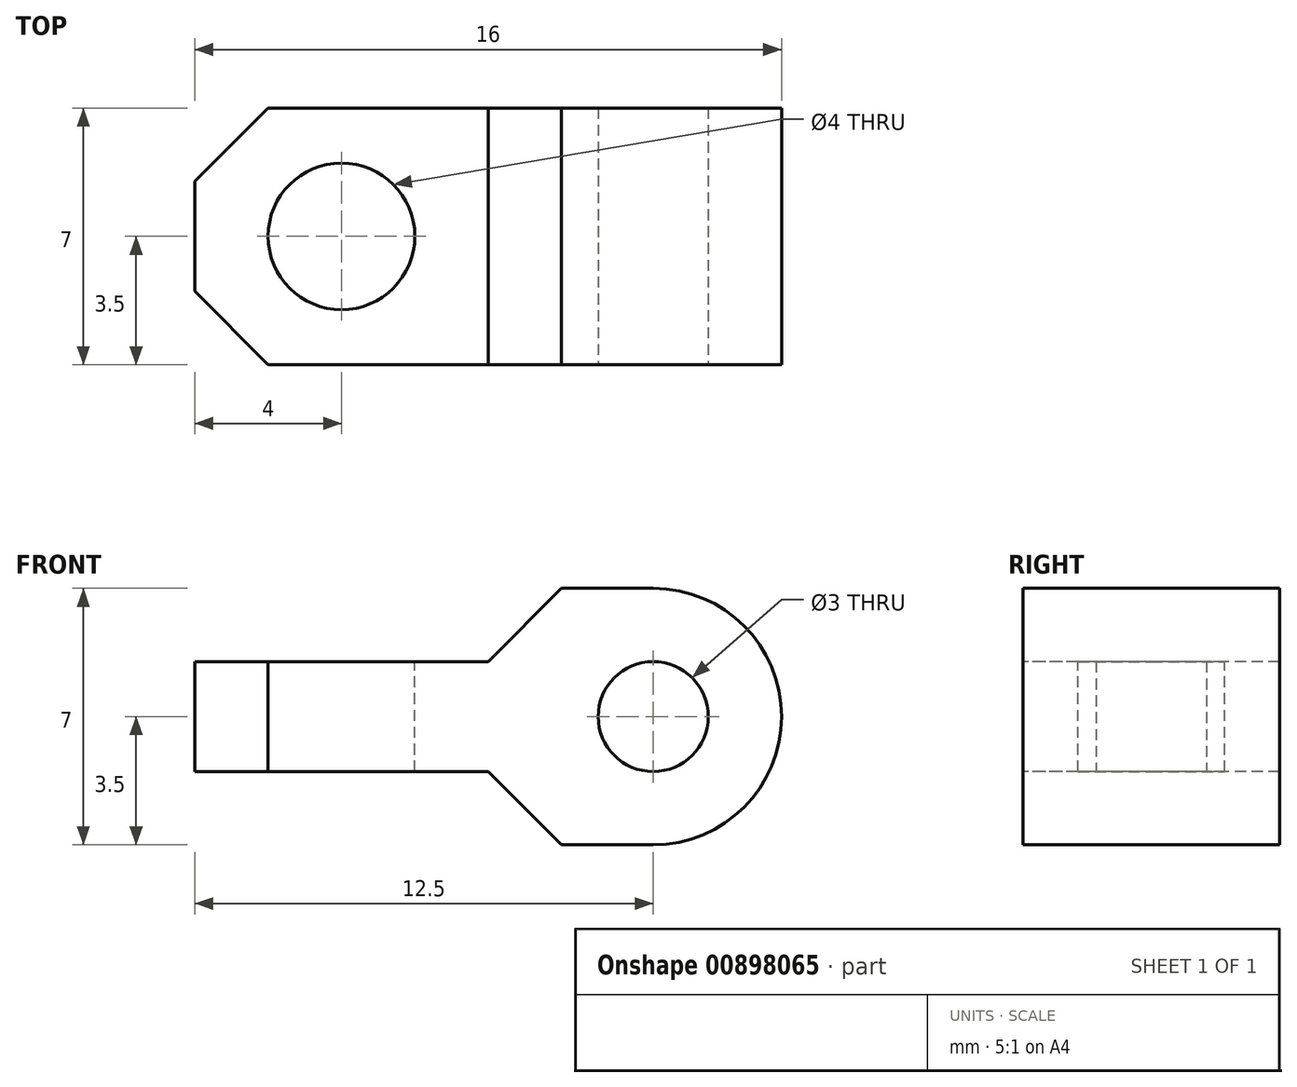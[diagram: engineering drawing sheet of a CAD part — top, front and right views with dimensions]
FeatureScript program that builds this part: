
annotation { "Feature Type Name" : "Feature", "Feature Type Description" : "" }
export const myFeature = defineFeature(function(context is Context, id is Id, definition is map)
    precondition{}
    {
        {
            var Q0;
            Q0=qCreatedBy(makeId("Top.planeOp"),FACE);
            var sketch = newSketch(context, id + "F0", { "sketchPlane" : qUnion([Q0])});
            skLineSegment(sketch, "E0", {"start": v(-3.1, 1.5) * mm, "end": v(-3.1, -1.5) * mm});
            skLineSegment(sketch, "E1", {"start": v(-3.1, -1.5) * mm, "end": v(-1.1, -3.5) * mm});
            skLineSegment(sketch, "E2", {"start": v(-1.1, -3.5) * mm, "end": v(12.9, -3.5) * mm});
            skLineSegment(sketch, "E3", {"start": v(12.9, -3.5) * mm, "end": v(12.9, 3.5) * mm});
            skLineSegment(sketch, "E4", {"start": v(12.9, 3.5) * mm, "end": v(-1.1, 3.5) * mm});
            skLineSegment(sketch, "E5", {"start": v(-1.1, 3.5) * mm, "end": v(-3.1, 1.5) * mm});
            skSolve(sketch);
        }
        {
            var Q0;
            Q0 = qSketchRegion(id + "F0", true);
            extrude(context, id + "F1", {"entities" : qUnion([Q0]), "endBound" : BoundingType.SYMMETRIC, "depth" : 3 * mm, "offsetDistance" : 25 * mm});
        }
        {
            var Q0;
            Q0=makeQuery(id+"F1.opExtrude","SWEPT_FACE",FACE,{"disambiguationData":[OSD([sQuery(id+"F0.wireOp",EDGE,"E2")])]});
            var sketch = newSketch(context, id + "F2", { "sketchPlane" : qUnion([Q0])});
            skLineSegment(sketch, "E6", {"start": v(4.9, 1.5) * mm, "end": v(6.9, 3.5) * mm});
            skLineSegment(sketch, "E7", {"start": v(6.9, 3.5) * mm, "end": v(12.9, 3.5) * mm});
            skLineSegment(sketch, "E8", {"start": v(12.9, 3.5) * mm, "end": v(12.9, 1.5) * mm});
            skLineSegment(sketch, "E9", {"start": v(12.9, 1.5) * mm, "end": v(4.9, 1.5) * mm});
            skLineSegment(sketch, "E10", {"start": v(4.9, -1.5) * mm, "end": v(12.9, -1.5) * mm});
            skLineSegment(sketch, "E11", {"start": v(12.9, -1.5) * mm, "end": v(12.9, -3.5) * mm});
            skLineSegment(sketch, "E12", {"start": v(12.9, -3.5) * mm, "end": v(6.9, -3.5) * mm});
            skLineSegment(sketch, "E13", {"start": v(6.9, -3.5) * mm, "end": v(4.9, -1.5) * mm});
            skSolve(sketch);
        }
        {
            var Q0;
            Q0 = qSketchRegion(id + "F2", true);
            extrude(context, id + "F3", {"entities" : qUnion([Q0]), "operationType" : NewBodyOperationType.ADD, "oppositeDirection" : true, "depth" : 7 * mm, "offsetDistance" : 25 * mm});
        }
        {
            var Q0;
            Q0=makeQuery(id+"F3.boolean.opBoolean","MERGE",FACE,{"derivedFrom":[makeQuery(id+"F1.opExtrude","SWEPT_FACE",FACE,{"disambiguationData":[OSD([sQuery(id+"F0.wireOp",EDGE,"E2")])]}),makeQuery(id+"F3.opExtrude","CAP_FACE",FACE,{"disambiguationData":[OSD([sQuery(id+"F2.wireOp",EDGE,"E6"),sQuery(id+"F2.wireOp",EDGE,"E7"),sQuery(id+"F2.wireOp",EDGE,"E8"),sQuery(id+"F2.wireOp",EDGE,"E9")])],"isStart":true}),makeQuery(id+"F3.opExtrude","CAP_FACE",FACE,{"disambiguationData":[OSD([sQuery(id+"F2.wireOp",EDGE,"E10"),sQuery(id+"F2.wireOp",EDGE,"E11"),sQuery(id+"F2.wireOp",EDGE,"E12"),sQuery(id+"F2.wireOp",EDGE,"E13")])],"isStart":true})]});
            var sketch = newSketch(context, id + "F4", { "sketchPlane" : qUnion([Q0])});
            skCircle(sketch, "E14", {"center": v(9.4, 0) * mm, "radius": 1.5 * mm});
            skSolve(sketch);
        }
        {
            var Q0;
            Q0 = qSketchRegion(id + "F4", true);
            extrude(context, id + "F5", {"entities" : qUnion([Q0]), "operationType" : NewBodyOperationType.REMOVE, "endBound" : BoundingType.THROUGH_ALL, "oppositeDirection" : true, "depth" : 25 * mm, "offsetDistance" : 25 * mm});
        }
        {
            var Q0;
            Q0=makeQuery(id+"F1.opExtrude","CAP_FACE",FACE,{"disambiguationData":[OSD([sQuery(id+"F0.wireOp",EDGE,"E0"),sQuery(id+"F0.wireOp",EDGE,"E1"),sQuery(id+"F0.wireOp",EDGE,"E2"),sQuery(id+"F0.wireOp",EDGE,"E3"),sQuery(id+"F0.wireOp",EDGE,"E4"),sQuery(id+"F0.wireOp",EDGE,"E5")])],"isStart":false});
            var sketch = newSketch(context, id + "F6", { "sketchPlane" : qUnion([Q0])});
            skCircle(sketch, "E15", {"center": v(0.9, 0) * mm, "radius": 2 * mm});
            skSolve(sketch);
        }
        {
            var Q0;
            Q0 = qSketchRegion(id + "F6", true);
            extrude(context, id + "F7", {"entities" : qUnion([Q0]), "operationType" : NewBodyOperationType.REMOVE, "endBound" : BoundingType.THROUGH_ALL, "oppositeDirection" : true, "depth" : 25 * mm, "offsetDistance" : 25 * mm});
        }
        {
            var Q0;
            Q0=makeQuery(id+"F3.boolean.opBoolean","MERGE",FACE,{"derivedFrom":[makeQuery(id+"F1.opExtrude","SWEPT_FACE",FACE,{"disambiguationData":[OSD([sQuery(id+"F0.wireOp",EDGE,"E2")])]}),makeQuery(id+"F3.opExtrude","CAP_FACE",FACE,{"disambiguationData":[OSD([sQuery(id+"F2.wireOp",EDGE,"E6"),sQuery(id+"F2.wireOp",EDGE,"E7"),sQuery(id+"F2.wireOp",EDGE,"E8"),sQuery(id+"F2.wireOp",EDGE,"E9")])],"isStart":true}),makeQuery(id+"F3.opExtrude","CAP_FACE",FACE,{"disambiguationData":[OSD([sQuery(id+"F2.wireOp",EDGE,"E10"),sQuery(id+"F2.wireOp",EDGE,"E11"),sQuery(id+"F2.wireOp",EDGE,"E12"),sQuery(id+"F2.wireOp",EDGE,"E13")])],"isStart":true})]});
            var sketch = newSketch(context, id + "F8", { "sketchPlane" : qUnion([Q0])});
            skArc(sketch, "E16", {"start": v(9.4, -3.5) * mm, "mid": v(12.9, 0) * mm, "end": v(9.4, 3.5) * mm});
            skLineSegment(sketch, "E17", {"start": v(12.9, 0) * mm, "end": v(12.9, 3.5) * mm});
            skLineSegment(sketch, "E18", {"start": v(12.9, 3.5) * mm, "end": v(9.4, 3.5) * mm});
            skLineSegment(sketch, "E19", {"start": v(12.9, 0) * mm, "end": v(12.9, -3.5) * mm});
            skLineSegment(sketch, "E20", {"start": v(12.9, -3.5) * mm, "end": v(9.4, -3.5) * mm});
            skSolve(sketch);
        }
        {
            var Q0;
            Q0 = qSketchRegion(id + "F8", true);
            extrude(context, id + "F9", {"entities" : qUnion([Q0]), "operationType" : NewBodyOperationType.REMOVE, "endBound" : BoundingType.THROUGH_ALL, "oppositeDirection" : true, "depth" : 25 * mm, "offsetDistance" : 25 * mm});
        }
    });
